# Revit family: Gleitplatten, V4A
name_source: partatom
category: HLS-Bauteile
revit_build: Autodesk Revit 2017 (Build: 20190507_1515(x64)
units: mm (PartAtom-declared; Revit-internal decimal feet)

## family parameters
Arbeitsebenenbasiert = Ja
Beim Laden mit Abzugskörper schneiden = Nein
Bemaßung runder Anschluss = Durchmesser verwenden
Gemeinsam genutzt = Ja
Immer vertikal = Nein
OmniClass-Nummer = 23.75.00.00
OmniClass-Titel = Climate Control (HVAC)
Raumberechnungspunkt = Nein
Teiletyp = Normal

## types (4) — shared parameters
Abstand zur Außenkante = 25 mm  [stored 0.082021 ft]
Achsmaß = 25 mm
Anschlüsse = 6kt-Mutter parametrik : Mutter M16 (4120522)
Anzahl Anschlüsse = 2
Fabrikat = MEFA
Firma = MEFA Befestigungs- und Montagesysteme GmbH
Höhe Gewindeanschluss HGW = 15 mm  [stored 0.0492126 ft]
Mengeneinheit = St
Stärke = 8 mm  [stored 0.0262467 ft]
vpe = 1 St
zero-valued in all types: Vorgabe-Ansicht

## per-type parameters (varying)
| type | Anschluss | Artikelnummer | Breite | EAN | Gewicht | Gewicht pro Bauteil | Kurztext1 | Kurztext2 | Länge | Muffe | max. zul. Last |
| Gleitplatte 200x100x 8, 2x M16, V4A | M16 | 0772832 | 100 mm  [stored 0.328084 ft] | 4250928418494 | 1.39 kg | 1.39 kg | Gleitplatte 200 x 100 x 8 V4A | Anschluss 2 x M16 | 200 mm  [stored 0.656168 ft] | 6kt-Mutter parametrik : Mutter M16 (4120522) | 4.50 kN |
| Gleitplatte 150x100x 8, 2x M16, V4A | M16 | 0772831 | 100 mm  [stored 0.328084 ft] | 4250928418487 | 1.06 kg | 1.06 kg | Gleitplatte 150 x 100 x 8 V4A | Anschluss 2 x M16 | 150 mm | 6kt-Mutter parametrik : Mutter M16 (4120522) | 6.80 kN |
| Gleitplatte 200x150x 8, 2x 1/2", V4A | 1/2'' | 0772824 | 150 mm | 4250928418470 | 2.03 kg | 2.03 kg | Gleitplatte 200 x 150 x 8 V4A | Anschluss 2 x 1/2'' | 200 mm  [stored 0.656168 ft] | Runde Gewindeanschlusse parametrik : A4 Schweißmuffe 1/2´´ | 6.80 kN |
| Gleitplatte 250x100x 8, 2x 1/2", V4A | 1/2'' | 0772823 | 100 mm  [stored 0.328084 ft] | 4250928418463 | 1.70 kg | 1.70 kg | Gleitplatte 250 x 100 x 8 V4A | Anschluss 2 x 1/2'' | 250 mm | Runde Gewindeanschlusse parametrik : A4 Schweißmuffe 1/2´´ | 3.40 kN |

note: [stored X ft] marks values corroborated as IEEE doubles in the binary element streams (Revit-internal decimal feet)

## geometry (parser evidence)
native form markers: Sweep x2
no freeform markers — native parametric forms only
